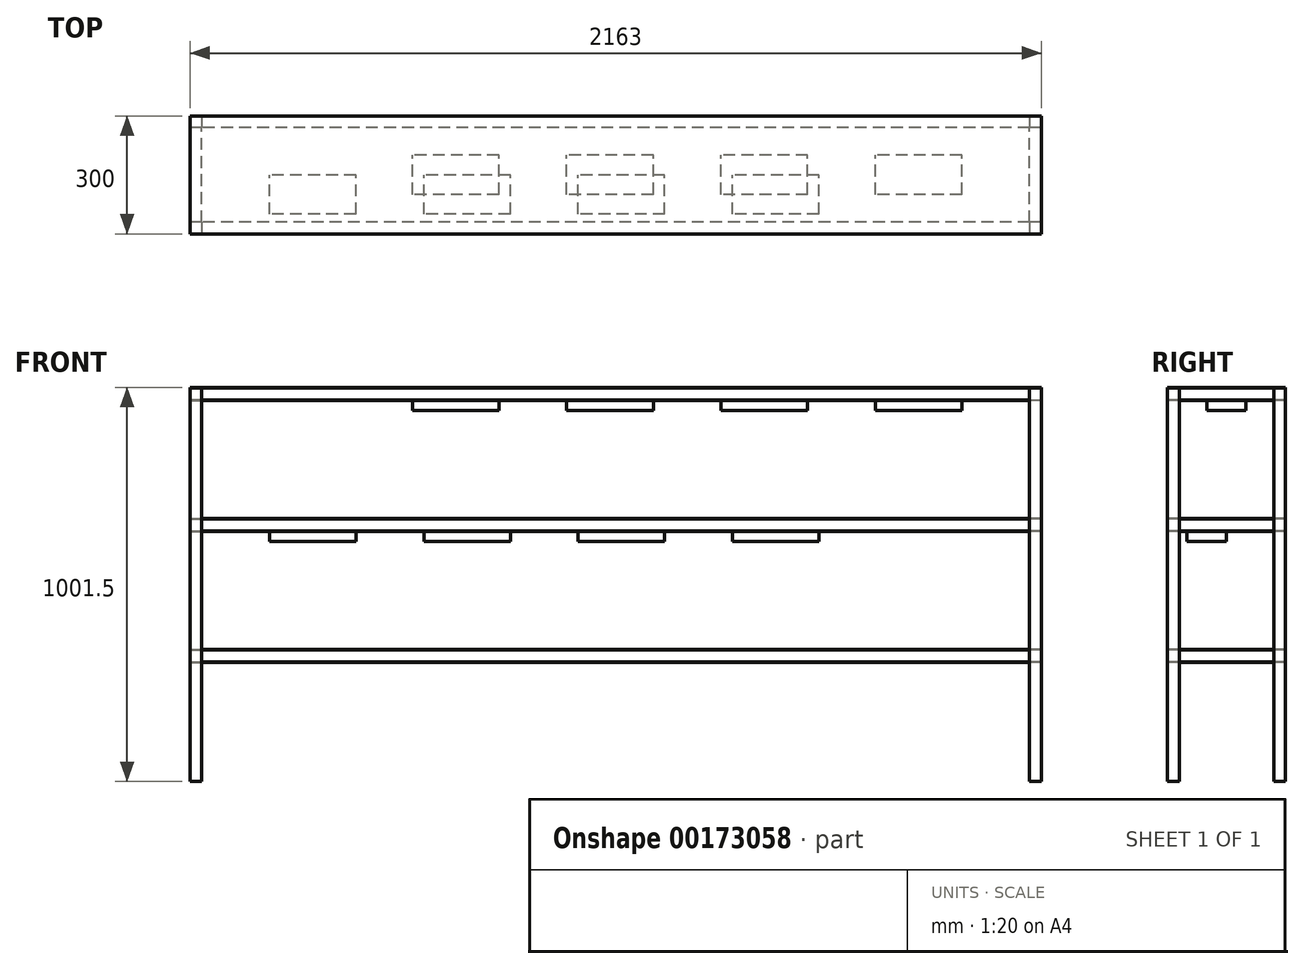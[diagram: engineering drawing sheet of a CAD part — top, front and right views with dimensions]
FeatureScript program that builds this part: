
annotation { "Feature Type Name" : "Feature", "Feature Type Description" : "" }
export const myFeature = defineFeature(function(context is Context, id is Id, definition is map)
    precondition{}
    {
        {
            var Q0;
            Q0=qCreatedBy(makeId("Top.planeOp"),FACE);
            var sketch = newSketch(context, id + "F0", { "sketchPlane" : qUnion([Q0])});
            skLineSegment(sketch, "E0.bottom", {"start": v(-1051.5, 150) * mm, "end": v(-1081.5, 150) * mm});
            skLineSegment(sketch, "E0.top", {"start": v(-1051.5, 120) * mm, "end": v(-1081.5, 120) * mm});
            skLineSegment(sketch, "E0.left", {"start": v(-1051.5, 150) * mm, "end": v(-1051.5, 120) * mm});
            skLineSegment(sketch, "E0.right", {"start": v(-1081.5, 150) * mm, "end": v(-1081.5, 120) * mm});
            skPoint(sketch, "E0.middle", {"position": v(-1066.5, 135) * mm});
            skLineSegment(sketch, "E1.bottom", {"start": v(1081.5, 150) * mm, "end": v(1051.5, 150) * mm});
            skLineSegment(sketch, "E1.top", {"start": v(1081.5, 120) * mm, "end": v(1051.5, 120) * mm});
            skLineSegment(sketch, "E1.left", {"start": v(1081.5, 150) * mm, "end": v(1081.5, 120) * mm});
            skLineSegment(sketch, "E1.right", {"start": v(1051.5, 150) * mm, "end": v(1051.5, 120) * mm});
            skPoint(sketch, "E1.middle", {"position": v(1066.5, 135) * mm});
            skLineSegment(sketch, "E2.bottom", {"start": v(1081.5, -120) * mm, "end": v(1051.5, -120) * mm});
            skLineSegment(sketch, "E2.top", {"start": v(1081.5, -150) * mm, "end": v(1051.5, -150) * mm});
            skLineSegment(sketch, "E2.left", {"start": v(1081.5, -120) * mm, "end": v(1081.5, -150) * mm});
            skLineSegment(sketch, "E2.right", {"start": v(1051.5, -120) * mm, "end": v(1051.5, -150) * mm});
            skPoint(sketch, "E2.middle", {"position": v(1066.5, -135) * mm});
            skPoint(sketch, "E2.middle.positionSnap0", {"position": v(1066.5, 120) * mm});
            skPoint(sketch, "E2.centerSnap0", {"position": v(1066.5, 120) * mm});
            skLineSegment(sketch, "E3.bottom", {"start": v(-1051.5, -120) * mm, "end": v(-1081.5, -120) * mm});
            skLineSegment(sketch, "E3.top", {"start": v(-1051.5, -150) * mm, "end": v(-1081.5, -150) * mm});
            skLineSegment(sketch, "E3.left", {"start": v(-1051.5, -120) * mm, "end": v(-1051.5, -150) * mm});
            skLineSegment(sketch, "E3.right", {"start": v(-1081.5, -120) * mm, "end": v(-1081.5, -150) * mm});
            skPoint(sketch, "E3.middle", {"position": v(-1066.5, -135) * mm});
            skPoint(sketch, "E3.middle.positionSnap0", {"position": v(-1066.5, 120) * mm});
            skPoint(sketch, "E3.middle.positionSnap1", {"position": v(1051.5, -135) * mm});
            skPoint(sketch, "E3.centerSnap0", {"position": v(-1066.5, 120) * mm});
            skPoint(sketch, "E3.centerSnap1", {"position": v(1051.5, -135) * mm});
            skSolve(sketch);
        }
        {
            var Q0;
            Q0 = qSketchRegion(id + "F0", true);
            extrude(context, id + "F1", {"entities" : qUnion([Q0]), "depth" : 1000 * mm});
        }
        {
            var Q0;
            Q0=qCreatedBy(makeId("Right.planeOp"),FACE);
            var sketch = newSketch(context, id + "F2", { "sketchPlane" : qUnion([Q0])});
            skLineSegment(sketch, "E4.bottom", {"start": v(-120, 1000) * mm, "end": v(-150, 1000) * mm});
            skLineSegment(sketch, "E4.top", {"start": v(-120, 970) * mm, "end": v(-150, 970) * mm});
            skLineSegment(sketch, "E4.left", {"start": v(-120, 1000) * mm, "end": v(-120, 970) * mm});
            skLineSegment(sketch, "E4.right", {"start": v(-150, 1000) * mm, "end": v(-150, 970) * mm});
            skPoint(sketch, "E4.middle", {"position": v(-135, 985) * mm});
            skLineSegment(sketch, "E5.bottom", {"start": v(150, 1000) * mm, "end": v(120, 1000) * mm});
            skLineSegment(sketch, "E5.top", {"start": v(150, 970) * mm, "end": v(120, 970) * mm});
            skLineSegment(sketch, "E5.left", {"start": v(150, 1000) * mm, "end": v(150, 970) * mm});
            skLineSegment(sketch, "E5.right", {"start": v(120, 1000) * mm, "end": v(120, 970) * mm});
            skPoint(sketch, "E5.middle", {"position": v(135, 985) * mm});
            skLineSegment(sketch, "E6.bottom", {"start": v(-120, 667) * mm, "end": v(-150, 667) * mm});
            skLineSegment(sketch, "E6.top", {"start": v(-120, 637) * mm, "end": v(-150, 637) * mm});
            skLineSegment(sketch, "E6.left", {"start": v(-120, 667) * mm, "end": v(-120, 637) * mm});
            skLineSegment(sketch, "E6.right", {"start": v(-150, 667) * mm, "end": v(-150, 637) * mm});
            skPoint(sketch, "E6.middle", {"position": v(-135, 652) * mm});
            skLineSegment(sketch, "E7.bottom", {"start": v(150, 667) * mm, "end": v(120, 667) * mm});
            skLineSegment(sketch, "E7.top", {"start": v(150, 637) * mm, "end": v(120, 637) * mm});
            skLineSegment(sketch, "E7.left", {"start": v(150, 667) * mm, "end": v(150, 637) * mm});
            skLineSegment(sketch, "E7.right", {"start": v(120, 667) * mm, "end": v(120, 637) * mm});
            skPoint(sketch, "E7.middle", {"position": v(135, 652) * mm});
            skPoint(sketch, "E7.middle.positionSnap0", {"position": v(135, 970) * mm});
            skPoint(sketch, "E7.centerSnap0", {"position": v(135, 970) * mm});
            skLineSegment(sketch, "E8.bottom", {"start": v(-120, 334) * mm, "end": v(-150, 334) * mm});
            skLineSegment(sketch, "E8.top", {"start": v(-120, 304) * mm, "end": v(-150, 304) * mm});
            skLineSegment(sketch, "E8.left", {"start": v(-120, 334) * mm, "end": v(-120, 304) * mm});
            skLineSegment(sketch, "E8.right", {"start": v(-150, 334) * mm, "end": v(-150, 304) * mm});
            skPoint(sketch, "E8.middle", {"position": v(-135, 319) * mm});
            skLineSegment(sketch, "E9.bottom", {"start": v(150, 334) * mm, "end": v(120, 334) * mm});
            skLineSegment(sketch, "E9.top", {"start": v(150, 304) * mm, "end": v(120, 304) * mm});
            skLineSegment(sketch, "E9.left", {"start": v(150, 334) * mm, "end": v(150, 304) * mm});
            skLineSegment(sketch, "E9.right", {"start": v(120, 334) * mm, "end": v(120, 304) * mm});
            skPoint(sketch, "E9.middle", {"position": v(135, 319) * mm});
            skSolve(sketch);
        }
        {
            var Q0;
            Q0 = qSketchRegion(id + "F2", true);
            extrude(context, id + "F3", {"entities" : qUnion([Q0]), "endBound" : BoundingType.UP_TO_NEXT, "depth" : 25 * mm, "hasSecondDirection" : true, "secondDirectionBound" : SecondDirectionBoundingType.UP_TO_NEXT, "secondDirectionOppositeDirection" : true, "secondDirectionDepth" : 25 * mm});
        }
        {
            var Q0;
            Q0=qCreatedBy(makeId("Front.planeOp"),FACE);
            var sketch = newSketch(context, id + "F4", { "sketchPlane" : qUnion([Q0])});
            skLineSegment(sketch, "E10.bottom", {"start": v(-1051.5, 1000) * mm, "end": v(-1081.5, 1000) * mm});
            skLineSegment(sketch, "E10.top", {"start": v(-1051.5, 970) * mm, "end": v(-1081.5, 970) * mm});
            skLineSegment(sketch, "E10.left", {"start": v(-1051.5, 1000) * mm, "end": v(-1051.5, 970) * mm});
            skLineSegment(sketch, "E10.right", {"start": v(-1081.5, 1000) * mm, "end": v(-1081.5, 970) * mm});
            skPoint(sketch, "E10.middle", {"position": v(-1066.5, 985) * mm});
            skLineSegment(sketch, "E11.bottom", {"start": v(1051.5, 1000) * mm, "end": v(1081.5, 1000) * mm});
            skLineSegment(sketch, "E11.top", {"start": v(1051.5, 970) * mm, "end": v(1081.5, 970) * mm});
            skLineSegment(sketch, "E11.left", {"start": v(1051.5, 1000) * mm, "end": v(1051.5, 970) * mm});
            skLineSegment(sketch, "E11.right", {"start": v(1081.5, 1000) * mm, "end": v(1081.5, 970) * mm});
            skPoint(sketch, "E11.middle", {"position": v(1066.5, 985) * mm});
            skLineSegment(sketch, "E12.bottom", {"start": v(-1051.5, 667) * mm, "end": v(-1081.5, 667) * mm});
            skLineSegment(sketch, "E12.top", {"start": v(-1051.5, 637) * mm, "end": v(-1081.5, 637) * mm});
            skLineSegment(sketch, "E12.left", {"start": v(-1051.5, 667) * mm, "end": v(-1051.5, 637) * mm});
            skLineSegment(sketch, "E12.right", {"start": v(-1081.5, 667) * mm, "end": v(-1081.5, 637) * mm});
            skPoint(sketch, "E12.middle", {"position": v(-1066.5, 652) * mm});
            skLineSegment(sketch, "E13.bottom", {"start": v(-1051.5, 334) * mm, "end": v(-1081.5, 334) * mm});
            skLineSegment(sketch, "E13.top", {"start": v(-1051.5, 304) * mm, "end": v(-1081.5, 304) * mm});
            skLineSegment(sketch, "E13.left", {"start": v(-1051.5, 334) * mm, "end": v(-1051.5, 304) * mm});
            skLineSegment(sketch, "E13.right", {"start": v(-1081.5, 334) * mm, "end": v(-1081.5, 304) * mm});
            skPoint(sketch, "E13.middle", {"position": v(-1066.5, 319) * mm});
            skPoint(sketch, "E13.middle.positionSnap0", {"position": v(-1066.5, 637) * mm});
            skPoint(sketch, "E13.cornerSnap0", {"position": v(-1051.5, 652) * mm});
            skPoint(sketch, "E13.centerSnap0", {"position": v(-1066.5, 637) * mm});
            skLineSegment(sketch, "E14.bottom", {"start": v(1081.5, 667) * mm, "end": v(1051.5, 667) * mm});
            skLineSegment(sketch, "E14.top", {"start": v(1081.5, 637) * mm, "end": v(1051.5, 637) * mm});
            skLineSegment(sketch, "E14.left", {"start": v(1081.5, 667) * mm, "end": v(1081.5, 637) * mm});
            skLineSegment(sketch, "E14.right", {"start": v(1051.5, 667) * mm, "end": v(1051.5, 637) * mm});
            skPoint(sketch, "E14.middle", {"position": v(1066.5, 652) * mm});
            skLineSegment(sketch, "E15.bottom", {"start": v(1081.5, 334) * mm, "end": v(1051.5, 334) * mm});
            skLineSegment(sketch, "E15.top", {"start": v(1081.5, 304) * mm, "end": v(1051.5, 304) * mm});
            skLineSegment(sketch, "E15.left", {"start": v(1081.5, 334) * mm, "end": v(1081.5, 304) * mm});
            skLineSegment(sketch, "E15.right", {"start": v(1051.5, 334) * mm, "end": v(1051.5, 304) * mm});
            skPoint(sketch, "E15.middle", {"position": v(1066.5, 319) * mm});
            skPoint(sketch, "E15.middle.positionSnap0", {"position": v(-1051.5, 319) * mm});
            skPoint(sketch, "E15.centerSnap0", {"position": v(-1051.5, 319) * mm});
            skSolve(sketch);
        }
        {
            var Q0;
            Q0 = qSketchRegion(id + "F4", true);
            extrude(context, id + "F5", {"entities" : qUnion([Q0]), "endBound" : BoundingType.UP_TO_NEXT, "depth" : 25 * mm, "hasSecondDirection" : true, "secondDirectionBound" : SecondDirectionBoundingType.UP_TO_NEXT, "secondDirectionOppositeDirection" : true, "secondDirectionDepth" : 25 * mm});
        }
        {
            var Q0;
            Q0=makeQuery(id+"F3.opExtrude","SWEPT_FACE",FACE,{"disambiguationData":[OSD([sQuery(id+"F2.wireOp",EDGE,"E8.bottom")])]});
            var sketch = newSketch(context, id + "F6", { "sketchPlane" : qUnion([Q0])});
            skLineSegment(sketch, "E16", {"start": v(-1081.5, 120) * mm, "end": v(-1051.5, 120) * mm});
            skLineSegment(sketch, "E17", {"start": v(-1051.5, 120) * mm, "end": v(-1051.5, 150) * mm});
            skLineSegment(sketch, "E18", {"start": v(-1051.5, 150) * mm, "end": v(1051.5, 150) * mm});
            skLineSegment(sketch, "E19", {"start": v(1051.5, 150) * mm, "end": v(1051.5, 120) * mm});
            skLineSegment(sketch, "E20", {"start": v(1051.5, 120) * mm, "end": v(1081.5, 120) * mm});
            skLineSegment(sketch, "E21", {"start": v(1081.5, 120) * mm, "end": v(1081.5, -120) * mm});
            skLineSegment(sketch, "E22", {"start": v(1081.5, -120) * mm, "end": v(1051.5, -120) * mm});
            skLineSegment(sketch, "E23", {"start": v(1051.5, -120) * mm, "end": v(1051.5, -150) * mm});
            skLineSegment(sketch, "E24", {"start": v(1051.5, -150) * mm, "end": v(-1051.5, -150) * mm});
            skLineSegment(sketch, "E25", {"start": v(-1051.5, -150) * mm, "end": v(-1051.5, -120) * mm});
            skLineSegment(sketch, "E26", {"start": v(-1051.5, -120) * mm, "end": v(-1081.5, -120) * mm});
            skLineSegment(sketch, "E27", {"start": v(-1081.5, -120) * mm, "end": v(-1081.5, 120) * mm});
            skSolve(sketch);
        }
        {
            var Q0;
            Q0 = qSketchRegion(id + "F6", true);
            extrude(context, id + "F7", {"entities" : qUnion([Q0]), "depth" : 1.5 * mm});
        }
        {
            var Q0;
            Q0=makeQuery(id+"F3.opExtrude","SWEPT_FACE",FACE,{"disambiguationData":[OSD([sQuery(id+"F2.wireOp",EDGE,"E6.bottom")])]});
            var sketch = newSketch(context, id + "F8", { "sketchPlane" : qUnion([Q0])});
            skLineSegment(sketch, "E28", {"start": v(-1081.5, 120) * mm, "end": v(-1051.5, 120) * mm});
            skLineSegment(sketch, "E29", {"start": v(-1051.5, 120) * mm, "end": v(-1051.5, 150) * mm});
            skLineSegment(sketch, "E30", {"start": v(-1051.5, 150) * mm, "end": v(1051.5, 150) * mm});
            skLineSegment(sketch, "E31", {"start": v(1051.5, 150) * mm, "end": v(1051.5, 120) * mm});
            skLineSegment(sketch, "E32", {"start": v(1051.5, 120) * mm, "end": v(1081.5, 120) * mm});
            skLineSegment(sketch, "E33", {"start": v(1081.5, 120) * mm, "end": v(1081.5, -120) * mm});
            skLineSegment(sketch, "E34", {"start": v(1081.5, -120) * mm, "end": v(1051.5, -120) * mm});
            skLineSegment(sketch, "E35", {"start": v(1051.5, -120) * mm, "end": v(1051.5, -150) * mm});
            skLineSegment(sketch, "E36", {"start": v(1051.5, -150) * mm, "end": v(-1051.5, -150) * mm});
            skLineSegment(sketch, "E37", {"start": v(-1051.5, -150) * mm, "end": v(-1051.5, -120) * mm});
            skLineSegment(sketch, "E38", {"start": v(-1051.5, -120) * mm, "end": v(-1081.5, -120) * mm});
            skLineSegment(sketch, "E39", {"start": v(-1081.5, -120) * mm, "end": v(-1081.5, 120) * mm});
            skSolve(sketch);
        }
        {
            var Q0;
            Q0 = qSketchRegion(id + "F8", true);
            extrude(context, id + "F9", {"entities" : qUnion([Q0]), "depth" : 1.5 * mm});
        }
        {
            var Q0;
            Q0=makeQuery(id+"F3.opExtrude","SWEPT_FACE",FACE,{"disambiguationData":[OSD([sQuery(id+"F2.wireOp",EDGE,"E4.bottom")])]});
            var sketch = newSketch(context, id + "F10", { "sketchPlane" : qUnion([Q0])});
            skLineSegment(sketch, "E40.bottom", {"start": v(-1081.5, 150) * mm, "end": v(1081.5, 150) * mm});
            skLineSegment(sketch, "E40.top", {"start": v(-1081.5, -150) * mm, "end": v(1081.5, -150) * mm});
            skLineSegment(sketch, "E40.left", {"start": v(-1081.5, 150) * mm, "end": v(-1081.5, -150) * mm});
            skLineSegment(sketch, "E40.right", {"start": v(1081.5, 150) * mm, "end": v(1081.5, -150) * mm});
            skSolve(sketch);
        }
        {
            var Q0;
            Q0 = qSketchRegion(id + "F10", true);
            extrude(context, id + "F11", {"entities" : qUnion([Q0]), "depth" : 1.5 * mm});
        }
        {
            var Q0;
            Q0=makeQuery(id+"F3.opExtrude","SWEPT_FACE",FACE,{"disambiguationData":[OSD([sQuery(id+"F2.wireOp",EDGE,"E8.top")])]});
            var sketch = newSketch(context, id + "F12", { "sketchPlane" : qUnion([Q0])});
            skLineSegment(sketch, "E41", {"start": v(-1081.5, 120) * mm, "end": v(-1051.5, 120) * mm});
            skLineSegment(sketch, "E42", {"start": v(-1051.5, 120) * mm, "end": v(-1051.5, 150) * mm});
            skLineSegment(sketch, "E43", {"start": v(-1051.5, 150) * mm, "end": v(1051.5, 150) * mm});
            skLineSegment(sketch, "E44", {"start": v(1051.5, 150) * mm, "end": v(1051.5, 120) * mm});
            skLineSegment(sketch, "E45", {"start": v(1051.5, 120) * mm, "end": v(1081.5, 120) * mm});
            skLineSegment(sketch, "E46", {"start": v(1081.5, 120) * mm, "end": v(1081.5, -120) * mm});
            skLineSegment(sketch, "E47", {"start": v(1081.5, -120) * mm, "end": v(1051.5, -120) * mm});
            skLineSegment(sketch, "E48", {"start": v(1051.5, -120) * mm, "end": v(1051.5, -150) * mm});
            skLineSegment(sketch, "E49", {"start": v(1051.5, -150) * mm, "end": v(-1051.5, -150) * mm});
            skLineSegment(sketch, "E50", {"start": v(-1051.5, -150) * mm, "end": v(-1051.5, -120) * mm});
            skLineSegment(sketch, "E51", {"start": v(-1051.5, -120) * mm, "end": v(-1081.5, -120) * mm});
            skLineSegment(sketch, "E52", {"start": v(-1081.5, -120) * mm, "end": v(-1081.5, 120) * mm});
            skSolve(sketch);
        }
        {
            var Q0;
            Q0 = qSketchRegion(id + "F12", true);
            extrude(context, id + "F13", {"entities" : qUnion([Q0]), "depth" : 1.5 * mm});
        }
        {
            var Q0;
            Q0=makeQuery(id+"F3.opExtrude","SWEPT_FACE",FACE,{"disambiguationData":[OSD([sQuery(id+"F2.wireOp",EDGE,"E6.top")])]});
            var sketch = newSketch(context, id + "F14", { "sketchPlane" : qUnion([Q0])});
            skLineSegment(sketch, "E53", {"start": v(-1081.5, 120) * mm, "end": v(-1051.5, 120) * mm});
            skLineSegment(sketch, "E54", {"start": v(-1051.5, 120) * mm, "end": v(-1051.5, 150) * mm});
            skLineSegment(sketch, "E55", {"start": v(-1051.5, 150) * mm, "end": v(1051.5, 150) * mm});
            skLineSegment(sketch, "E56", {"start": v(1051.5, 150) * mm, "end": v(1051.5, 120) * mm});
            skLineSegment(sketch, "E57", {"start": v(1051.5, 120) * mm, "end": v(1081.5, 120) * mm});
            skLineSegment(sketch, "E58", {"start": v(1081.5, 120) * mm, "end": v(1081.5, -120) * mm});
            skLineSegment(sketch, "E59", {"start": v(1081.5, -120) * mm, "end": v(1051.5, -120) * mm});
            skLineSegment(sketch, "E60", {"start": v(1051.5, -120) * mm, "end": v(1051.5, -150) * mm});
            skLineSegment(sketch, "E61", {"start": v(1051.5, -150) * mm, "end": v(-1051.5, -150) * mm});
            skLineSegment(sketch, "E62", {"start": v(-1051.5, -150) * mm, "end": v(-1051.5, -120) * mm});
            skLineSegment(sketch, "E63", {"start": v(-1051.5, -120) * mm, "end": v(-1081.5, -120) * mm});
            skLineSegment(sketch, "E64", {"start": v(-1081.5, -120) * mm, "end": v(-1081.5, 120) * mm});
            skSolve(sketch);
        }
        {
            var Q0;
            Q0 = qSketchRegion(id + "F14", true);
            extrude(context, id + "F15", {"entities" : qUnion([Q0]), "depth" : 1.5 * mm});
        }
        {
            var Q0;
            Q0=makeQuery(id+"F3.opExtrude","SWEPT_FACE",FACE,{"disambiguationData":[OSD([sQuery(id+"F2.wireOp",EDGE,"E4.top")])]});
            var sketch = newSketch(context, id + "F16", { "sketchPlane" : qUnion([Q0])});
            skLineSegment(sketch, "E65", {"start": v(-1081.5, 120) * mm, "end": v(-1051.5, 120) * mm});
            skLineSegment(sketch, "E66", {"start": v(-1051.5, 120) * mm, "end": v(-1051.5, 150) * mm});
            skLineSegment(sketch, "E67", {"start": v(-1051.5, 150) * mm, "end": v(1051.5, 150) * mm});
            skLineSegment(sketch, "E68", {"start": v(1051.5, 150) * mm, "end": v(1051.5, 120) * mm});
            skLineSegment(sketch, "E69", {"start": v(1051.5, 120) * mm, "end": v(1081.5, 120) * mm});
            skLineSegment(sketch, "E70", {"start": v(1081.5, 120) * mm, "end": v(1081.5, -120) * mm});
            skLineSegment(sketch, "E71", {"start": v(1081.5, -120) * mm, "end": v(1051.5, -120) * mm});
            skLineSegment(sketch, "E72", {"start": v(1051.5, -120) * mm, "end": v(1051.5, -150) * mm});
            skLineSegment(sketch, "E73", {"start": v(1051.5, -150) * mm, "end": v(-1051.5, -150) * mm});
            skLineSegment(sketch, "E74", {"start": v(-1051.5, -150) * mm, "end": v(-1051.5, -120) * mm});
            skLineSegment(sketch, "E75", {"start": v(-1051.5, -120) * mm, "end": v(-1081.5, -120) * mm});
            skLineSegment(sketch, "E76", {"start": v(-1081.5, -120) * mm, "end": v(-1081.5, 120) * mm});
            skSolve(sketch);
        }
        {
            var Q0;
            Q0 = qSketchRegion(id + "F16", true);
            extrude(context, id + "F17", {"entities" : qUnion([Q0]), "depth" : 1.5 * mm});
        }
        {
            var Q0;
            Q0=makeQuery(id+"F17.opExtrude","CAP_FACE",FACE,{"disambiguationData":[OSD([sQuery(id+"F16.wireOp",EDGE,"E65"),sQuery(id+"F16.wireOp",EDGE,"E66"),sQuery(id+"F16.wireOp",EDGE,"E67"),sQuery(id+"F16.wireOp",EDGE,"E68"),sQuery(id+"F16.wireOp",EDGE,"E69"),sQuery(id+"F16.wireOp",EDGE,"E70"),sQuery(id+"F16.wireOp",EDGE,"E71"),sQuery(id+"F16.wireOp",EDGE,"E72"),sQuery(id+"F16.wireOp",EDGE,"E73"),sQuery(id+"F16.wireOp",EDGE,"E74"),sQuery(id+"F16.wireOp",EDGE,"E75"),sQuery(id+"F16.wireOp",EDGE,"E76")])],"isStart":false});
            var sketch = newSketch(context, id + "F18", { "sketchPlane" : qUnion([Q0])});
            skLineSegment(sketch, "E77.bottom", {"start": v(-296.5, 50) * mm, "end": v(-516.5, 50) * mm});
            skLineSegment(sketch, "E77.top", {"start": v(-296.5, -50) * mm, "end": v(-516.5, -50) * mm});
            skLineSegment(sketch, "E77.left", {"start": v(-296.5, 50) * mm, "end": v(-296.5, -50) * mm});
            skLineSegment(sketch, "E77.right", {"start": v(-516.5, 50) * mm, "end": v(-516.5, -50) * mm});
            skPoint(sketch, "E77.middle", {"position": v(-406.5, 0) * mm});
            skLineSegment(sketch, "E78.bottom", {"start": v(95.5, 50) * mm, "end": v(-124.5, 50) * mm});
            skLineSegment(sketch, "E78.top", {"start": v(95.5, -50) * mm, "end": v(-124.5, -50) * mm});
            skLineSegment(sketch, "E78.left", {"start": v(95.5, 50) * mm, "end": v(95.5, -50) * mm});
            skLineSegment(sketch, "E78.right", {"start": v(-124.5, 50) * mm, "end": v(-124.5, -50) * mm});
            skPoint(sketch, "E78.middle", {"position": v(-14.5, 0) * mm});
            skLineSegment(sketch, "E79.bottom", {"start": v(487.5, 50) * mm, "end": v(267.5, 50) * mm});
            skLineSegment(sketch, "E79.top", {"start": v(487.5, -50) * mm, "end": v(267.5, -50) * mm});
            skLineSegment(sketch, "E79.left", {"start": v(487.5, 50) * mm, "end": v(487.5, -50) * mm});
            skLineSegment(sketch, "E79.right", {"start": v(267.5, 50) * mm, "end": v(267.5, -50) * mm});
            skPoint(sketch, "E79.middle", {"position": v(377.5, 0) * mm});
            skLineSegment(sketch, "E80.bottom", {"start": v(879.5, 50) * mm, "end": v(659.5, 50) * mm});
            skLineSegment(sketch, "E80.top", {"start": v(879.5, -50) * mm, "end": v(659.5, -50) * mm});
            skLineSegment(sketch, "E80.left", {"start": v(879.5, 50) * mm, "end": v(879.5, -50) * mm});
            skLineSegment(sketch, "E80.right", {"start": v(659.5, 50) * mm, "end": v(659.5, -50) * mm});
            skPoint(sketch, "E80.middle", {"position": v(769.5, 0) * mm});
            skSolve(sketch);
        }
        {
            var Q0;
            Q0 = qSketchRegion(id + "F18", true);
            extrude(context, id + "F19", {"entities" : qUnion([Q0]), "operationType" : NewBodyOperationType.ADD, "depth" : 25 * mm});
        }
        {
            var Q0;
            Q0=makeQuery(id+"F15.opExtrude","CAP_FACE",FACE,{"disambiguationData":[OSD([sQuery(id+"F14.wireOp",EDGE,"E53"),sQuery(id+"F14.wireOp",EDGE,"E54"),sQuery(id+"F14.wireOp",EDGE,"E55"),sQuery(id+"F14.wireOp",EDGE,"E56"),sQuery(id+"F14.wireOp",EDGE,"E57"),sQuery(id+"F14.wireOp",EDGE,"E58"),sQuery(id+"F14.wireOp",EDGE,"E59"),sQuery(id+"F14.wireOp",EDGE,"E60"),sQuery(id+"F14.wireOp",EDGE,"E61"),sQuery(id+"F14.wireOp",EDGE,"E62"),sQuery(id+"F14.wireOp",EDGE,"E63"),sQuery(id+"F14.wireOp",EDGE,"E64")])],"isStart":false});
            var sketch = newSketch(context, id + "F20", { "sketchPlane" : qUnion([Q0])});
            skLineSegment(sketch, "E81.bottom", {"start": v(-659.5, 100) * mm, "end": v(-879.5, 100) * mm});
            skLineSegment(sketch, "E81.top", {"start": v(-659.5, 0) * mm, "end": v(-879.5, 0) * mm});
            skLineSegment(sketch, "E81.left", {"start": v(-659.5, 100) * mm, "end": v(-659.5, 0) * mm});
            skLineSegment(sketch, "E81.right", {"start": v(-879.5, 100) * mm, "end": v(-879.5, 0) * mm});
            skPoint(sketch, "E81.middle", {"position": v(-769.5, 50) * mm});
            skLineSegment(sketch, "E82.bottom", {"start": v(-267.5, 100) * mm, "end": v(-487.5, 100) * mm});
            skLineSegment(sketch, "E82.top", {"start": v(-267.5, 0) * mm, "end": v(-487.5, 0) * mm});
            skLineSegment(sketch, "E82.left", {"start": v(-267.5, 100) * mm, "end": v(-267.5, 0) * mm});
            skLineSegment(sketch, "E82.right", {"start": v(-487.5, 100) * mm, "end": v(-487.5, 0) * mm});
            skPoint(sketch, "E82.middle", {"position": v(-377.5, 50) * mm});
            skLineSegment(sketch, "E83.bottom", {"start": v(124.5, 100) * mm, "end": v(-95.5, 100) * mm});
            skLineSegment(sketch, "E83.top", {"start": v(124.5, 0) * mm, "end": v(-95.5, 0) * mm});
            skLineSegment(sketch, "E83.left", {"start": v(124.5, 100) * mm, "end": v(124.5, 0) * mm});
            skLineSegment(sketch, "E83.right", {"start": v(-95.5, 100) * mm, "end": v(-95.5, 0) * mm});
            skPoint(sketch, "E83.middle", {"position": v(14.5, 50) * mm});
            skLineSegment(sketch, "E84.bottom", {"start": v(516.5, 100) * mm, "end": v(296.5, 100) * mm});
            skLineSegment(sketch, "E84.top", {"start": v(516.5, 0) * mm, "end": v(296.5, 0) * mm});
            skLineSegment(sketch, "E84.left", {"start": v(516.5, 100) * mm, "end": v(516.5, 0) * mm});
            skLineSegment(sketch, "E84.right", {"start": v(296.5, 100) * mm, "end": v(296.5, 0) * mm});
            skPoint(sketch, "E84.middle", {"position": v(406.5, 50) * mm});
            skSolve(sketch);
        }
        {
            var Q0;
            Q0 = qSketchRegion(id + "F20", true);
            extrude(context, id + "F21", {"entities" : qUnion([Q0]), "operationType" : NewBodyOperationType.ADD, "depth" : 25 * mm});
        }
    });
